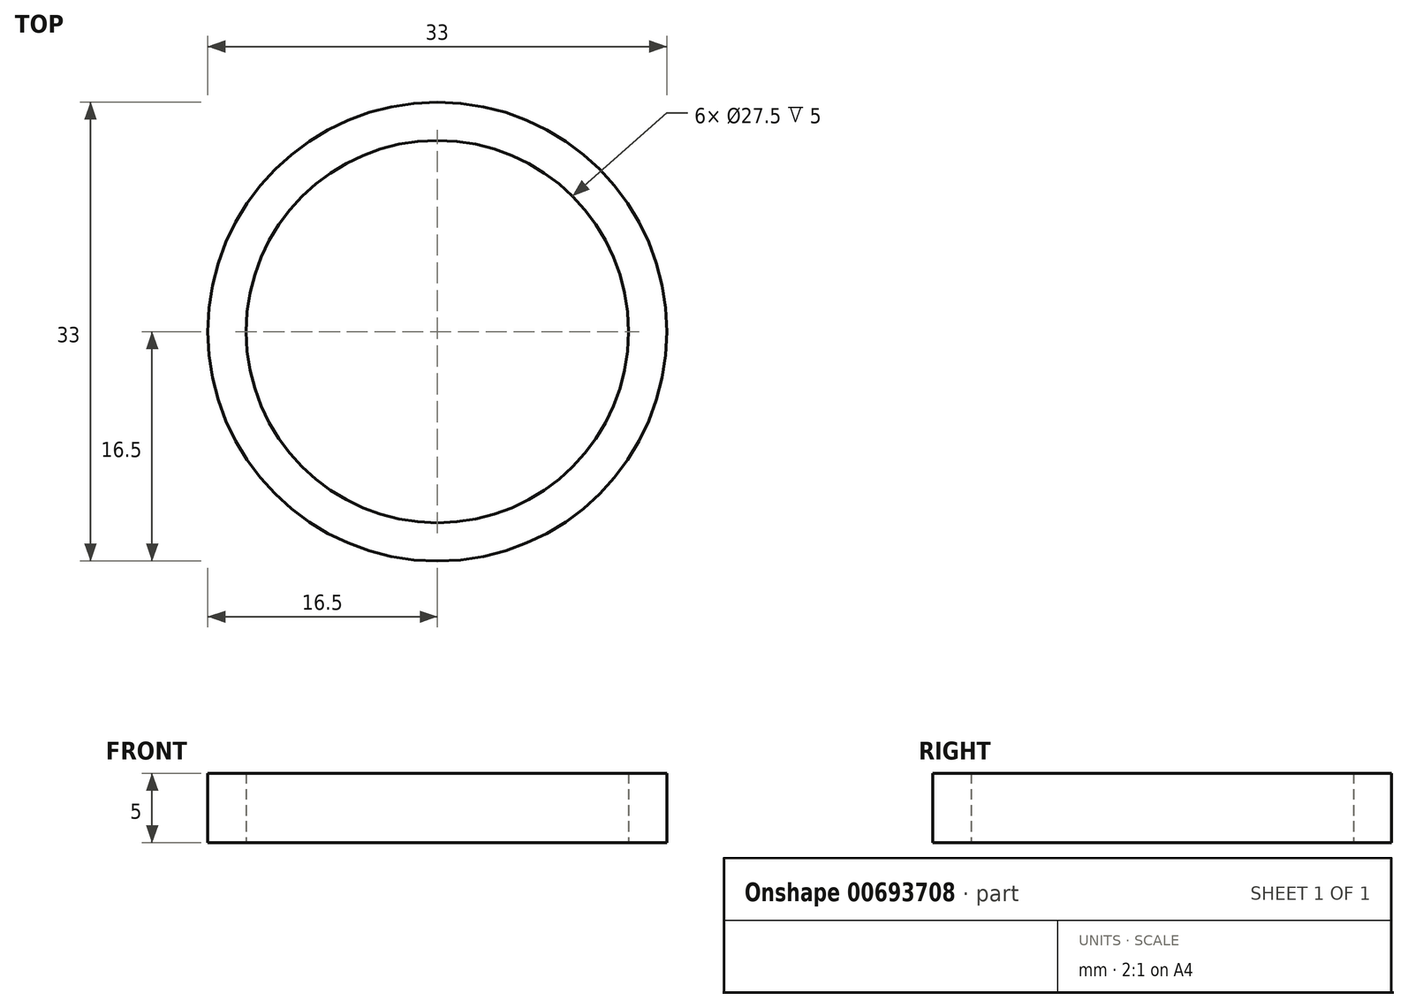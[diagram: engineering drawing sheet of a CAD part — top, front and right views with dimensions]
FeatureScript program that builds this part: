
annotation { "Feature Type Name" : "Feature", "Feature Type Description" : "" }
export const myFeature = defineFeature(function(context is Context, id is Id, definition is map)
    precondition{}
    {
        {
            var Q0;
            Q0=qCreatedBy(makeId("Top.planeOp"),FACE);
            var sketch = newSketch(context, id + "F0", { "sketchPlane" : qUnion([Q0])});
            skCircle(sketch, "E0", {"center": v(0, 0) * mm, "radius": 13.75 * mm});
            skCircle(sketch, "E1", {"center": v(0, 0) * mm, "radius": 16.5 * mm});
            skSolve(sketch);
        }
        {
            var Q0;
            Q0=makeQuery(id+"F0.imprint","IMPRINT",FACE,{"disambiguationData":[TD([[makeQuery(id+"F0.imprint","IMPRINT",EDGE,{"derivedFrom":sQuery(id+"F0.wireOp",EDGE,"E0")}),-1.0]])]});
            extrude(context, id + "F1", {"entities" : qUnion([Q0]), "depth" : 5 * mm, "offsetDistance" : 25 * mm});
        }
    });
